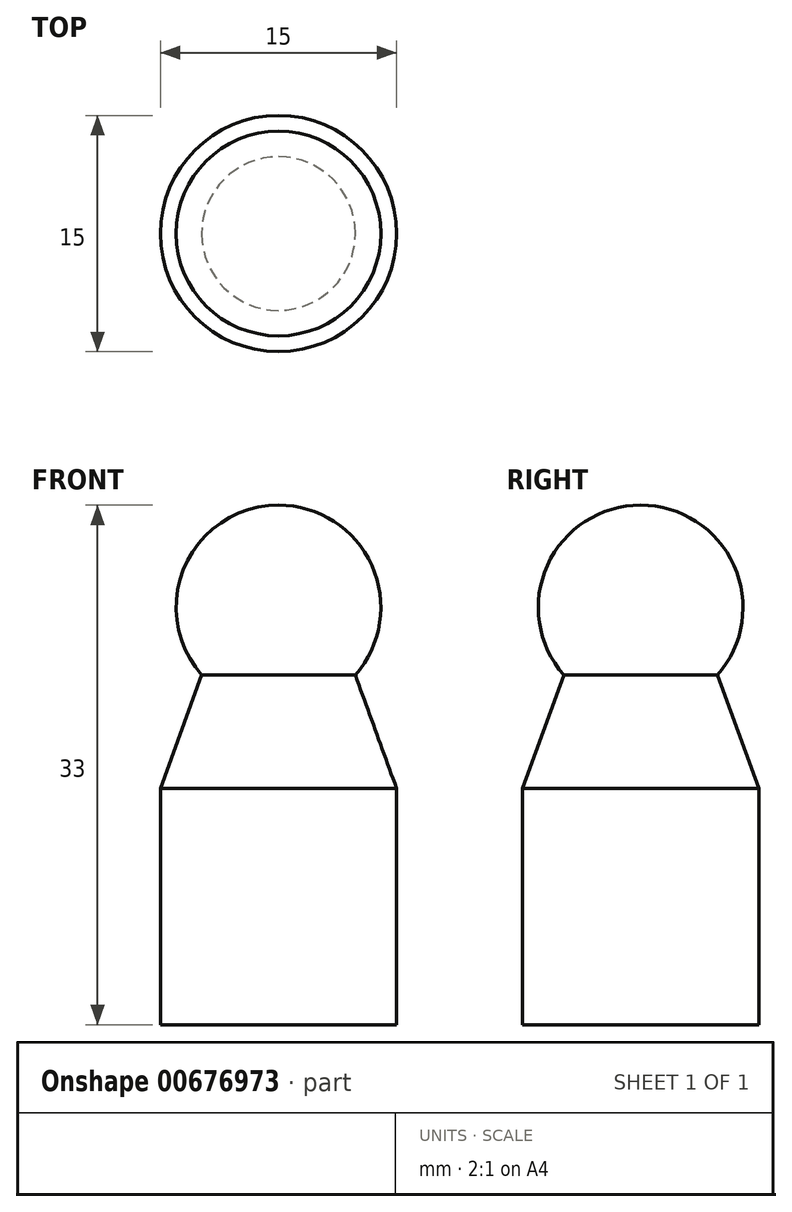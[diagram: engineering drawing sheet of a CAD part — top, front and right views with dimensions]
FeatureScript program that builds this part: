
annotation { "Feature Type Name" : "Feature", "Feature Type Description" : "" }
export const myFeature = defineFeature(function(context is Context, id is Id, definition is map)
    precondition{}
    {
        {
            var Q0;
            Q0=qCreatedBy(makeId("Top.planeOp"),FACE);
            var sketch = newSketch(context, id + "F0", { "sketchPlane" : qUnion([Q0])});
            skCircle(sketch, "E0", {"center": v(0, 0) * mm, "radius": 7.5 * mm});
            skSolve(sketch);
        }
        {
            var Q0;
            Q0=qSketchRegion(id+"F0",true);
            extrude(context, id + "F1", {"entities" : qUnion([Q0]), "depth" : 15 * mm, "offsetDistance" : 25 * mm});
        }
        {
            var Q0;
            Q0=makeQuery(id+"F1.opExtrude","CAP_FACE",FACE,{"disambiguationData":[OSD([sQuery(id+"F0.wireOp",EDGE,"E0")])],"isStart":false});
            var Q1;
            Q1 = qSketchRegion(id + "F3", true);
            extrude(context, id + "F2", {"entities" : qUnion([Q0, Q1]), "operationType" : NewBodyOperationType.ADD, "depth" : 10 * mm, "offsetDistance" : 25 * mm, "hasDraft" : true, "draftAngle" : 20 * degree, "draftPullDirection" : true});
        }
        {
            var Q0;
            Q0=qCreatedBy(makeId("Front.planeOp"),FACE);
            var sketch = newSketch(context, id + "F3", { "sketchPlane" : qUnion([Q0])});
            skArc(sketch, "E1", {"start": v(0, 20) * mm, "mid": v(6.5, 26.5) * mm, "end": v(0, 33) * mm});
            skLineSegment(sketch, "E2.0", {"start": v(-7.5, 15) * mm, "end": v(7.5, 15) * mm, "construction": true});
            skLineSegment(sketch, "E3", {"start": v(0, 20) * mm, "end": v(0, 33) * mm});
            skSolve(sketch);
        }
        {
            var Q0;
            Q0=qSketchRegion(id+"F3",true);
            var Q1;
            Q1=sQuery(id+"F3.wireOp",EDGE,"E3");
            revolve(context, id + "F4", {"operationType" : NewBodyOperationType.ADD, "entities" : qUnion([Q0]), "axis" : qUnion([Q1]), "revolveType" : RevolveType.FULL});
        }
    });
